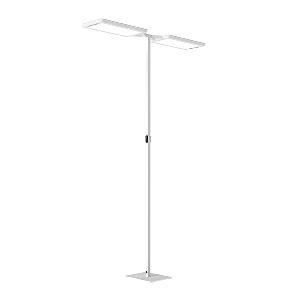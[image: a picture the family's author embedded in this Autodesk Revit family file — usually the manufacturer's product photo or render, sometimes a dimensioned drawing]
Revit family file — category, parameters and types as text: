
# Revit family: yara_doublet_-_yts_2_15000_vtl_rx_ws_cee_s0_c_114268000-00808483_f0f7
name_source: partatom
category: Lighting Fixtures
units: mm (PartAtom-declared; Revit-internal decimal feet)

## family parameters
Cut with Voids When Loaded = No
Host = Face
Light Source = No
Part Type = Normal
Room Calculation Point = No
Round Connector Dimension = Use Diameter
Shared = No

## types (1)
- YARA.doubleT - YTS 2/15000/VTL/RX/WS/CEE/S0/C (1 x LED, 15000 lm, VTL)
    Apparent Load = 214 VA
    Approval mark = CE
    CIE Flux Codes = 58 87 97 13 100
    Color Rendering = 80-89
    Color Temperature = VTL
    Control Gear = Electronic ballast
    Default Elevation = 1800 mm
    Description = YTS 2/15000/VTL/RX/WS/CEE/S0/R|Free-standing luminaire|light source: LED Daylight 2700-6500 K  Energy efficiency category A/A+/A++|work equipment: Electronic ballast DALI|connected load: 220-240 V, 50/60 Hz|Power consumption: approx. 210 W|power factor: approx. 0,966|luminous flux: 30000 lm|luminous efficacy: 142 lm/W|light distribution: Direct/indirect|direct ratio: approx. 13 %|color rendering index (CRI): >= 80|chromaticity tolerance:  3 SDCM|technology: Multiple daylight-dependent motion sensors|operation: Wireless switch|luminaire body|material: Aluminium/plastic|surface: Powder coatet|colour: White|lamp cover: Acrylic (PMMA), Satine, Structured|tubular section|material: Steel tube|surface: Powder-coated|Form: Tubular section upright|colour of tubular section: White|luminaire base|Form: Rectangular flat|weight (net): approx. 24.0 kg|mains lead: 3.00 m Mains plug CEE 7/VII|Fastening: Floor standing base|glare control: Conical prismatic screen|luminance(L65): <= 2700 cd/m|unified glare rating(4H 8H): <=  16|special features: App control, Asymmetric radiation, Biodynamic light VTL, Direct and indirect lighting component with edge light and light guidetechnology for a homogeneous light exit, Flicker-free, LTX multisensor for workplace optimisation, Magnetic control panel, freely positionable, Optional LTX Cloud connection, TALK Bluetooth|Approval mark: VDE - ENEC|
    Frequency = 50 Hz, 60 Hz
    Height = 24 mm  [stored 0.0787402 ft]
    Lamp = 1 x LED
    Lamp Light Flux = 15000 lm
    Lamp count = 1
    Length = 690 mm
    Luminous efficacy = 140 lm/W
    Manufacturer = Waldmann
    ModVariant = No
    Model = 114268000-00808483
    Mounting Place = Floor
    Mounting Type = Freestanding
    Number of Poles = 1
    OnlyDefault = Yes
    Power Factor = 1
    Product Name = YARA.doubleT - YTS 2/15000/VTL/RX/WS/CEE/S0/C
    Product group = Free standing luminaire
    ProductGroupID = 13
    Protection Class = Protection class I
    Protection Degree = IP 20
    RLX_Detail_Level = 1
    RlxData = <blob elided: 63321 chars, md5=5f5ba948>
    Socket = socket
    Standby Power = 0 W
    System Light Flux = 30000 lm
    System Power = 214 W
    Type Comments = Product without accessories
    Type Image = yts-rx-ws-r.jpg
    URL = http://relux.com
    VarID = ---
    Voltage = 230 V
    Voltage Range = 220-240 V
    Weight = 0.00 kg
    Width = 358 mm

note: [stored X ft] marks values corroborated as IEEE doubles in the binary element streams (Revit-internal decimal feet)

## geometry (parser evidence)
native form markers: Blend x4, Sweep x17
no freeform markers — native parametric forms only
